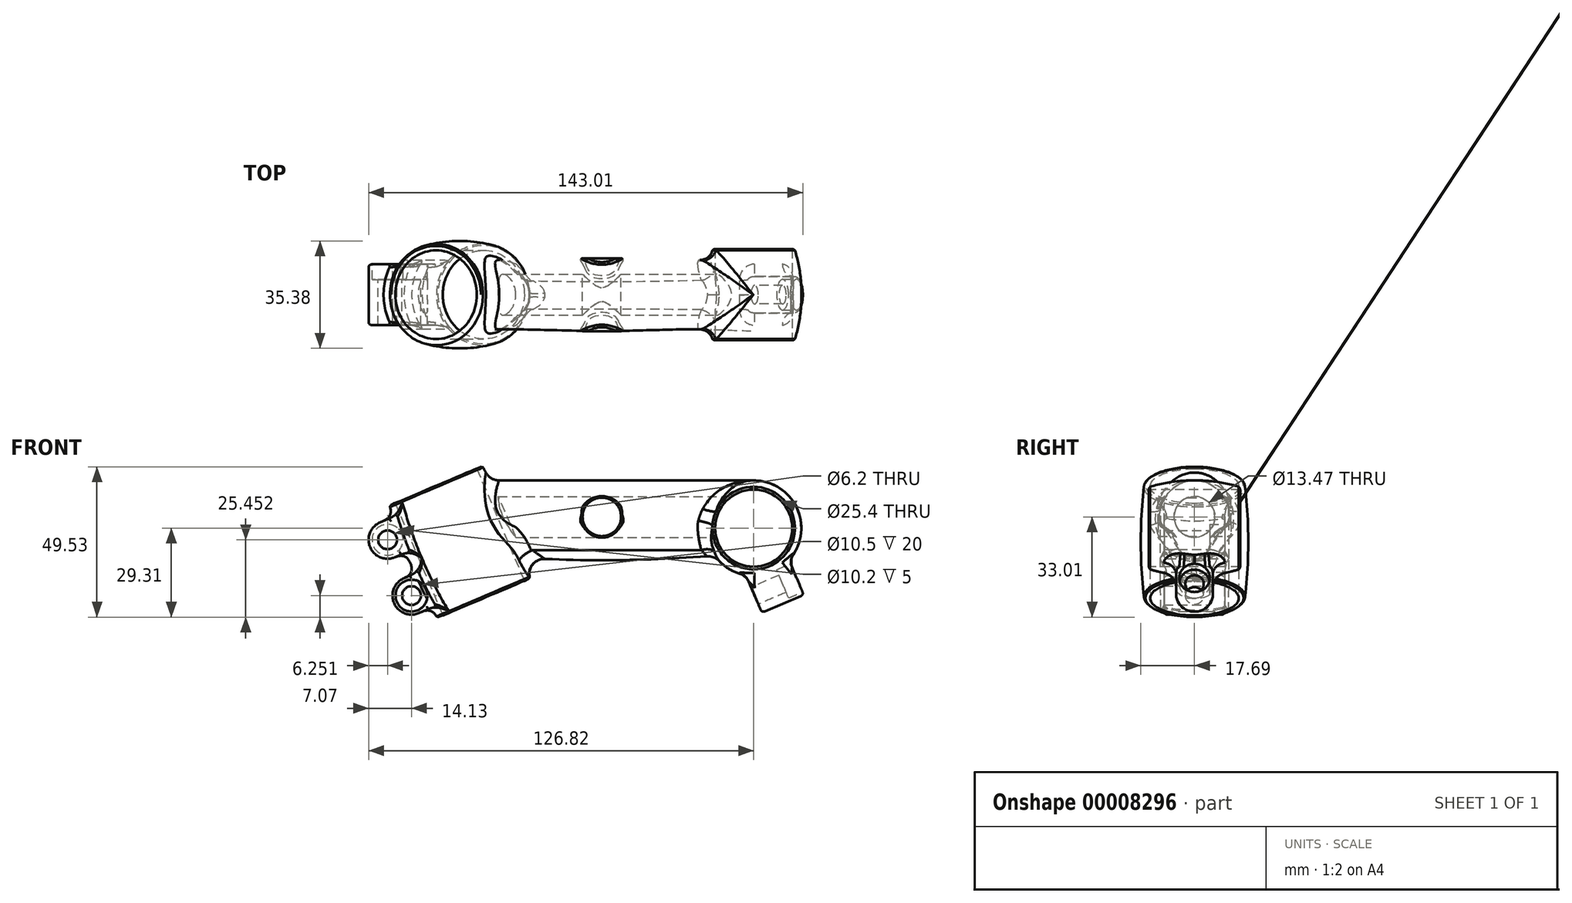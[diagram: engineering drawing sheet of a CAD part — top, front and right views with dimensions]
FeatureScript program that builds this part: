
annotation { "Feature Type Name" : "Feature", "Feature Type Description" : "" }
export const myFeature = defineFeature(function(context is Context, id is Id, definition is map)
    precondition{}
    {
        {
            var Q0;
            Q0=qCreatedBy(makeId("Right.planeOp"),FACE);
            var sketch = newSketch(context, id + "F0", { "sketchPlane" : qUnion([Q0])});
            skArc(sketch, "E0", {"start": v(11.9, 1.57) * mm, "mid": v(-0.17, 12) * mm, "end": v(-11.94, 1.24) * mm});
            skArc(sketch, "E1", {"start": v(-4.75, -11.02) * mm, "mid": v(-5.92, -6.75) * mm, "end": v(-9.19, -3.76) * mm});
            skArc(sketch, "E2.0.MirrorCS", {"start": v(4.18, -11.25) * mm, "mid": v(5.4, -6.72) * mm, "end": v(8.95, -3.66) * mm});
            skArc(sketch, "E3", {"start": v(-4.75, -11.02) * mm, "mid": v(-0.37, -14.28) * mm, "end": v(4.18, -11.25) * mm});
            skPoint(sketch, "E4.visualSharp", {"position": v(-11.62, -3) * mm});
            skArc(sketch, "E4.filletArc", {"start": v(-11.94, 1.24) * mm, "mid": v(-11.34, -1.69) * mm, "end": v(-9.19, -3.76) * mm});
            skPoint(sketch, "E5.visualSharp", {"position": v(11.62, -3) * mm});
            skArc(sketch, "E5.filletArc", {"start": v(8.95, -3.66) * mm, "mid": v(11.3, -1.53) * mm, "end": v(11.9, 1.57) * mm});
            skLineSegment(sketch, "E6", {"start": v(0, -14.28) * mm, "end": v(0, 12) * mm, "construction": true});
            skLineSegment(sketch, "E7", {"start": v(11.85, 0) * mm, "end": v(-11.91, 0) * mm, "construction": true});
            skSolve(sketch);
        }
        {
            var Q0;
            Q0=qCreatedBy(makeId("Right.planeOp"),FACE);
            cPlane(context, id + "F1", {"entities" : qUnion([Q0]), "cplaneType" : CPlaneType.OFFSET, "offset" : 50 * mm, "width" : 150 * mm, "height" : 150 * mm});
        }
        {
            var Q0;
            Q0=qCreatedBy(id+"F1.planeOp",FACE);
            var sketch = newSketch(context, id + "F2", { "sketchPlane" : qUnion([Q0])});
            skCircle(sketch, "E8", {"center": v(0, 0) * mm, "radius": 12 * mm});
            skLineSegment(sketch, "E9", {"start": v(0, -12) * mm, "end": v(0, 12) * mm, "construction": true});
            skLineSegment(sketch, "E10", {"start": v(-12, 0) * mm, "end": v(12, 0) * mm, "construction": true});
            skSolve(sketch);
        }
        {
            var Q0;
            Q0=qCreatedBy(makeId("Right.planeOp"),FACE);
            cPlane(context, id + "F3", {"entities" : qUnion([Q0]), "cplaneType" : CPlaneType.OFFSET, "offset" : 50 * mm, "oppositeDirection" : true, "width" : 150 * mm, "height" : 150 * mm});
        }
        {
            var Q0;
            Q0=qCreatedBy(id+"F3.planeOp",FACE);
            var sketch = newSketch(context, id + "F4", { "sketchPlane" : qUnion([Q0])});
            skCircle(sketch, "E11", {"center": v(0, 0) * mm, "radius": 12 * mm});
            skLineSegment(sketch, "E12", {"start": v(0, -12) * mm, "end": v(0, 12) * mm, "construction": true});
            skLineSegment(sketch, "E13", {"start": v(12, 0) * mm, "end": v(-12, 0) * mm, "construction": true});
            skSolve(sketch);
        }
        {
            var Q0;
            Q0=makeQuery(id+"F2.imprint","IMPRINT",FACE,{"disambiguationData":[TD([[makeQuery(id+"F2.imprint","IMPRINT",EDGE,{"derivedFrom":sQuery(id+"F2.wireOp",EDGE,"E8")}),1.0]])]});
            var Q1;
            Q1=makeQuery(id+"F0.imprint","IMPRINT",FACE,{"disambiguationData":[TD([[makeQuery(id+"F0.imprint","IMPRINT",EDGE,{"derivedFrom":sQuery(id+"F0.wireOp",EDGE,"E0")}),1.0]])]});
            var Q2;
            Q2=makeQuery(id+"F4.imprint","IMPRINT",FACE,{"disambiguationData":[TD([[makeQuery(id+"F4.imprint","IMPRINT",EDGE,{"derivedFrom":sQuery(id+"F4.wireOp",EDGE,"E11")}),1.0]])]});
            var Q3;
            Q3=sQuery(id+"F4.wireOp",VERTEX,"E12.end");
            var Q4;
            Q4=sQuery(id+"F0.wireOp",VERTEX,"E6.end");
            var Q5;
            Q5=sQuery(id+"F2.wireOp",VERTEX,"E9.end");
            loft(context, id + "F5", {"sheetProfilesArray" : [{ "sheetProfileEntities" : qUnion([Q0]) }, { "sheetProfileEntities" : qUnion([Q1]) }, { "sheetProfileEntities" : qUnion([Q2]) }], "matchConnections" : true, "connections" : [{ "connectionEntities" : qUnion([Q3, Q4, Q5]), "connectionEdgeQueries" : qUnion([]), "connectionEdgeParameters" : [] }]});
        }
        {
            var Q0;
            Q0=qCreatedBy(id+"F1.planeOp",FACE);
            var sketch = newSketch(context, id + "F6", { "sketchPlane" : qUnion([Q0])});
            skLineSegment(sketch, "E14", {"start": v(0, 0) * mm, "end": v(0, 7) * mm});
            skLineSegment(sketch, "E15.0", {"start": v(0, 9) * mm, "end": v(15, 9) * mm, "construction": true});
            skLineSegment(sketch, "E16.0", {"start": v(0, -3.7) * mm, "end": v(30.55, -3.7) * mm});
            skPoint(sketch, "E17.start.orphan", {"position": v(0, 14.9) * mm});
            skLineSegment(sketch, "E18", {"start": v(15, 9) * mm, "end": v(15, 7) * mm});
            skArc(sketch, "E19", {"start": v(15, 9) * mm, "mid": v(14.9, 9.49) * mm, "end": v(14.6, 9.9) * mm});
            skArc(sketch, "E20", {"start": v(14.6, 9.9) * mm, "mid": v(7.38, 11.53) * mm, "end": v(0, 12) * mm});
            skLineSegment(sketch, "E21.0", {"start": v(0, 7) * mm, "end": v(15, 7) * mm});
            skArc(sketch, "E22.0.MirrorCS", {"start": v(-14.6, 9.9) * mm, "mid": v(-7.38, 11.53) * mm, "end": v(0, 12) * mm});
            skArc(sketch, "E23.0.MirrorCS", {"start": v(-15, 9) * mm, "mid": v(-14.9, 9.49) * mm, "end": v(-14.6, 9.9) * mm});
            skLineSegment(sketch, "E24.0.MirrorCS", {"start": v(-15, 9) * mm, "end": v(-15, 7) * mm});
            skLineSegment(sketch, "E25.0.MirrorCS", {"start": v(0, 7) * mm, "end": v(-15, 7) * mm});
            skSolve(sketch);
        }
        {
            var Q0;
            Q0 = qSketchRegion(id + "F6", true);
            var Q1;
            Q1=sQuery(id+"F6.wireOp",EDGE,"E16.0");
            revolve(context, id + "F7", {"operationType" : NewBodyOperationType.ADD, "entities" : qUnion([Q0]), "axis" : qUnion([Q1]), "revolveType" : RevolveType.FULL});
        }
        {
            var Q0;
            Q0=makeQuery(id+"F7.opRevolve","SWEPT_FACE",FACE,{"disambiguationData":[OSD([sQuery(id+"F6.wireOp",EDGE,"E24.0.MirrorCS")])]});
            var sketch = newSketch(context, id + "F8", { "sketchPlane" : qUnion([Q0])});
            skCircle(sketch, "E26", {"center": v(50, -3.7) * mm, "radius": 12.7 * mm});
            skSolve(sketch);
        }
        {
            var Q0;
            Q0 = qSketchRegion(id + "F8", true);
            extrude(context, id + "F9", {"entities" : qUnion([Q0]), "operationType" : NewBodyOperationType.REMOVE, "oppositeDirection" : true, "depth" : 30 * mm});
        }
        {
            var Q0;
            Q0=qCreatedBy(makeId("Front.planeOp"),FACE);
            var sketch = newSketch(context, id + "F10", { "sketchPlane" : qUnion([Q0])});
            skLineSegment(sketch, "E27", {"start": v(11.01, 21.07) * mm, "end": v(-86.9, -12.65) * mm});
            skPoint(sketch, "E28.orphan", {"position": v(-50.17, 0) * mm});
            skSolve(sketch);
        }
        {
            var Q0;
            Q0=qCreatedBy(id+"F1.planeOp",FACE);
            var sketch = newSketch(context, id + "F11", { "sketchPlane" : qUnion([Q0])});
            skCircle(sketch, "E29", {"center": v(0, 0) * mm, "radius": 6.73 * mm});
            skSolve(sketch);
        }
        {
            var Q0;
            Q0 = qSketchRegion(id + "F11", true);
            extrude(context, id + "F12", {"entities" : qUnion([Q0]), "operationType" : NewBodyOperationType.REMOVE, "oppositeDirection" : true, "depth" : 100 * mm});
        }
        {
            var Q0;
            Q0=makeQuery(id+"F7.opRevolve","SWEPT_EDGE",EDGE,{"disambiguationData":[OSD([sQuery(id+"F6.wireOp",EDGE,"E20"),sQuery(id+"F6.wireOp",EDGE,"E22.0.MirrorCS")])]});
            var Q1;
            Q1=makeQuery(id+"F7.boolean.opBoolean","INTERSECT",EDGE,{"derivedFrom":[makeQuery(id+"F5.opLoft","SWEPT_FACE",FACE,{"disambiguationData":[OSD([sQuery(id+"F0.wireOp",EDGE,"E1"),sQuery(id+"F0.wireOp",EDGE,"E2.0.MirrorCS"),sQuery(id+"F0.wireOp",EDGE,"E3"),sQuery(id+"F0.wireOp",EDGE,"E4.filletArc"),sQuery(id+"F2.wireOp",EDGE,"E8")])]}),makeQuery(id+"F7.opRevolve","SWEPT_FACE",FACE,{"disambiguationData":[OSD([sQuery(id+"F6.wireOp",EDGE,"E22.0.MirrorCS")])]})]});
            var Q2;
            Q2=makeQuery(id+"F7.boolean.opBoolean","INTERSECT",EDGE,{"derivedFrom":[makeQuery(id+"F5.opLoft","SWEPT_FACE",FACE,{"disambiguationData":[OSD([sQuery(id+"F0.wireOp",EDGE,"E1"),sQuery(id+"F0.wireOp",EDGE,"E2.0.MirrorCS"),sQuery(id+"F0.wireOp",EDGE,"E3"),sQuery(id+"F0.wireOp",EDGE,"E4.filletArc"),sQuery(id+"F2.wireOp",EDGE,"E8")])]}),makeQuery(id+"F7.opRevolve","SWEPT_FACE",FACE,{"disambiguationData":[OSD([sQuery(id+"F6.wireOp",EDGE,"E20")])]})]});
            var Q3;
            Q3=makeQuery(id+"F7.boolean.opBoolean","INTERSECT",EDGE,{"derivedFrom":[makeQuery(id+"F5.opLoft","SWEPT_FACE",FACE,{"disambiguationData":[OSD([sQuery(id+"F0.wireOp",EDGE,"E1"),sQuery(id+"F0.wireOp",EDGE,"E2.0.MirrorCS"),sQuery(id+"F0.wireOp",EDGE,"E3"),sQuery(id+"F0.wireOp",EDGE,"E5.filletArc"),sQuery(id+"F2.wireOp",EDGE,"E8")])]}),makeQuery(id+"F7.opRevolve","SWEPT_FACE",FACE,{"disambiguationData":[OSD([sQuery(id+"F6.wireOp",EDGE,"E22.0.MirrorCS")])]})]});
            var Q4;
            Q4=makeQuery(id+"F7.boolean.opBoolean","INTERSECT",EDGE,{"derivedFrom":[makeQuery(id+"F5.opLoft","SWEPT_FACE",FACE,{"disambiguationData":[OSD([sQuery(id+"F0.wireOp",EDGE,"E1"),sQuery(id+"F0.wireOp",EDGE,"E2.0.MirrorCS"),sQuery(id+"F0.wireOp",EDGE,"E3"),sQuery(id+"F0.wireOp",EDGE,"E5.filletArc"),sQuery(id+"F2.wireOp",EDGE,"E8")])]}),makeQuery(id+"F7.opRevolve","SWEPT_FACE",FACE,{"disambiguationData":[OSD([sQuery(id+"F6.wireOp",EDGE,"E20")])]})]});
            fillet(context, id + "F13", {"entities" : qUnion([Q0, Q1, Q2, Q3, Q4]), "radius" : 5 * mm, "tangentPropagation" : true, "allowEdgeOverflow" : false});
        }
        {
            var Q0;
            Q0=sQuery(id+"F10.wireOp",EDGE,"E27");
            cPlane(context, id + "F14", {"entities" : qUnion([Q0]), "cplaneType" : CPlaneType.LINE_ANGLE, "offset" : 150 * mm, "angle" : 0 * degree, "width" : 150 * mm, "height" : 150 * mm});
        }
        {
            var Q0;
            Q0=qCreatedBy(id+"F14.planeOp",FACE);
            var sketch = newSketch(context, id + "F15", { "sketchPlane" : qUnion([Q0])});
            skLineSegment(sketch, "E30", {"start": v(-34.95, -36.2) * mm, "end": v(-56.16, 13.8) * mm});
            skPoint(sketch, "E31.orphan", {"position": v(-50.3, 0) * mm});
            skLineSegment(sketch, "E32.0", {"start": v(12.64, 16.34) * mm, "end": v(-85.27, -17.37) * mm, "construction": true});
            skLineSegment(sketch, "E33.0", {"start": v(-68.04, 4.42) * mm, "end": v(-69.93, 3.77) * mm});
            skLineSegment(sketch, "E34.0", {"start": v(-52.38, -32.49) * mm, "end": v(-54.27, -33.14) * mm});
            skLineSegment(sketch, "E35", {"start": v(-68.04, 4.42) * mm, "end": v(-52.38, -32.49) * mm, "construction": true});
            skArc(sketch, "E36", {"start": v(-69.93, 3.77) * mm, "mid": v(-63.11, -15.11) * mm, "end": v(-54.27, -33.14) * mm});
            skLineSegment(sketch, "E37", {"start": v(-52.38, -32.49) * mm, "end": v(-38.94, -26.79) * mm});
            skLineSegment(sketch, "E38", {"start": v(-68.04, 4.42) * mm, "end": v(-54.6, 10.12) * mm});
            skSolve(sketch);
        }
        {
            var Q0;
            Q0 = qSketchRegion(id + "F15", true);
            var Q1;
            Q1=sQuery(id+"F15.wireOp",EDGE,"E30");
            revolve(context, id + "F16", {"operationType" : NewBodyOperationType.ADD, "entities" : qUnion([Q0]), "axis" : qUnion([Q1]), "revolveType" : RevolveType.FULL});
        }
        {
            var Q0;
            Q0=makeQuery(id+"F16.opRevolve","SWEPT_FACE",FACE,{"disambiguationData":[OSD([sQuery(id+"F15.wireOp",EDGE,"E33.0")])]});
            cPlane(context, id + "F17", {"entities" : qUnion([Q0]), "cplaneType" : CPlaneType.LINE_ANGLE, "offset" : 5 * mm, "angle" : 180 * degree, "width" : 150 * mm, "height" : 150 * mm});
        }
        {
            var Q0;
            Q0=qCreatedBy(id+"F14.planeOp",FACE);
            var sketch = newSketch(context, id + "F18", { "sketchPlane" : qUnion([Q0])});
            skLineSegment(sketch, "E39", {"start": v(-69.95, 3.7) * mm, "end": v(-54.11, -33.26) * mm, "construction": true});
            skLineSegment(sketch, "E40", {"start": v(-57.44, -12.8) * mm, "end": v(-62.03, -14.78) * mm});
            skLineSegment(sketch, "E41.0", {"start": v(-61.38, -3.62) * mm, "end": v(-65.97, -5.59) * mm});
            skLineSegment(sketch, "E42.0", {"start": v(-74.55, 1.73) * mm, "end": v(-58.7, -35.23) * mm, "construction": true});
            skCircle(sketch, "E43", {"center": v(-70.57, -7.56) * mm, "radius": 3.1 * mm});
            skCircle(sketch, "E44", {"center": v(-70.57, -7.56) * mm, "radius": 5.25 * mm});
            skLineSegment(sketch, "E45.0", {"start": v(-65.36, 5.67) * mm, "end": v(-49.52, -31.29) * mm});
            skCircle(sketch, "E46.0", {"center": v(-70.57, -7.56) * mm, "radius": 6.25 * mm});
            skCircle(sketch, "E47.2.MirrorC", {"center": v(-62.69, -25.94) * mm, "radius": 3.1 * mm});
            skCircle(sketch, "E47.3.MirrorC", {"center": v(-62.69, -25.94) * mm, "radius": 5.25 * mm});
            skCircle(sketch, "E47.4.MirrorC", {"center": v(-62.69, -25.94) * mm, "radius": 6.25 * mm});
            skLineSegment(sketch, "E48", {"start": v(-73.03, -1.81) * mm, "end": v(-63.84, 2.13) * mm});
            skLineSegment(sketch, "E49", {"start": v(-65.15, -20.2) * mm, "end": v(-55.96, -16.26) * mm});
            skLineSegment(sketch, "E50", {"start": v(-60.23, -31.68) * mm, "end": v(-51.04, -27.75) * mm});
            skLineSegment(sketch, "E51", {"start": v(-68.1, -13.3) * mm, "end": v(-58.92, -9.36) * mm});
            skSolve(sketch);
        }
        {
            var Q0;
            Q0 = qSketchRegion(id + "F18", true);
            var Q1;
            Q1=makeQuery(id+"F18.imprint","IMPRINT",FACE,{"disambiguationData":[TD([[makeQuery(id+"F18.imprint","IMPRINT",EDGE,{"derivedFrom":sQuery(id+"F18.wireOp",EDGE,"E43")}),-1.0]])]});
            var Q2;
            Q2=makeQuery(id+"F18.imprint","IMPRINT",FACE,{"disambiguationData":[TD([[makeQuery(id+"F18.imprint","IMPRINT",EDGE,{"derivedFrom":sQuery(id+"F18.wireOp",EDGE,"E47.2.MirrorC")}),1.0]])]});
            extrude(context, id + "F19", {"entities" : qUnion([Q0, Q1, Q2]), "operationType" : NewBodyOperationType.ADD, "endBound" : BoundingType.SYMMETRIC, "depth" : 20 * mm});
        }
        {
            var Q0;
            Q0=makeQuery(id+"F19.boolean.opBoolean","INTERSECT",EDGE,{"derivedFrom":[makeQuery(id+"F16.boolean.opBoolean","SPLIT",FACE,{"disambiguationData":[TD([makeQuery(id+"F16.opRevolve","SWEPT_FACE",FACE,{"disambiguationData":[OSD([sQuery(id+"F15.wireOp",EDGE,"E33.0")])]})])],"derivedFrom":makeQuery(id+"F16.opRevolve","SWEPT_FACE",FACE,{"disambiguationData":[OSD([sQuery(id+"F15.wireOp",EDGE,"E36")])]})}),makeQuery(id+"F19.opExtrude","SWEPT_FACE",FACE,{"disambiguationData":[OSD([sQuery(id+"F18.wireOp",EDGE,"E49")])]})]});
            var Q1;
            Q1=makeQuery(id+"F19.boolean.opBoolean","INTERSECT",EDGE,{"derivedFrom":[makeQuery(id+"F16.boolean.opBoolean","SPLIT",FACE,{"disambiguationData":[TD([makeQuery(id+"F16.opRevolve","SWEPT_FACE",FACE,{"disambiguationData":[OSD([sQuery(id+"F15.wireOp",EDGE,"E33.0")])]})])],"derivedFrom":makeQuery(id+"F16.opRevolve","SWEPT_FACE",FACE,{"disambiguationData":[OSD([sQuery(id+"F15.wireOp",EDGE,"E36")])]})}),makeQuery(id+"F19.opExtrude","CAP_FACE",FACE,{"disambiguationData":[OSD([sQuery(id+"F18.wireOp",EDGE,"E45.0"),sQuery(id+"F18.wireOp",EDGE,"E47.2.MirrorC"),sQuery(id+"F18.wireOp",EDGE,"E47.4.MirrorC"),sQuery(id+"F18.wireOp",EDGE,"E49"),sQuery(id+"F18.wireOp",EDGE,"E50")])],"isStart":false})]});
            var Q2;
            Q2=makeQuery(id+"F19.boolean.opBoolean","INTERSECT",EDGE,{"derivedFrom":[makeQuery(id+"F16.boolean.opBoolean","SPLIT",FACE,{"disambiguationData":[TD([makeQuery(id+"F16.opRevolve","SWEPT_FACE",FACE,{"disambiguationData":[OSD([sQuery(id+"F15.wireOp",EDGE,"E33.0")])]})])],"derivedFrom":makeQuery(id+"F16.opRevolve","SWEPT_FACE",FACE,{"disambiguationData":[OSD([sQuery(id+"F15.wireOp",EDGE,"E36")])]})}),makeQuery(id+"F19.opExtrude","SWEPT_FACE",FACE,{"disambiguationData":[OSD([sQuery(id+"F18.wireOp",EDGE,"E50")])]})]});
            var Q3;
            Q3=makeQuery(id+"F19.boolean.opBoolean","INTERSECT",EDGE,{"derivedFrom":[makeQuery(id+"F16.boolean.opBoolean","SPLIT",FACE,{"disambiguationData":[TD([makeQuery(id+"F16.opRevolve","SWEPT_FACE",FACE,{"disambiguationData":[OSD([sQuery(id+"F15.wireOp",EDGE,"E33.0")])]})])],"derivedFrom":makeQuery(id+"F16.opRevolve","SWEPT_FACE",FACE,{"disambiguationData":[OSD([sQuery(id+"F15.wireOp",EDGE,"E36")])]})}),makeQuery(id+"F19.opExtrude","CAP_FACE",FACE,{"disambiguationData":[OSD([sQuery(id+"F18.wireOp",EDGE,"E45.0"),sQuery(id+"F18.wireOp",EDGE,"E47.2.MirrorC"),sQuery(id+"F18.wireOp",EDGE,"E47.4.MirrorC"),sQuery(id+"F18.wireOp",EDGE,"E49"),sQuery(id+"F18.wireOp",EDGE,"E50")])],"isStart":true})]});
            fillet(context, id + "F20", {"entities" : qUnion([Q0, Q1, Q2, Q3]), "radius" : 3.75 * mm, "tangentPropagation" : true, "rho" : 0.5, "crossSection" : FilletCrossSection.CONIC, "allowEdgeOverflow" : false});
        }
        {
            var Q0;
            Q0=makeQuery(id+"F19.boolean.opBoolean","INTERSECT",EDGE,{"derivedFrom":[makeQuery(id+"F16.boolean.opBoolean","SPLIT",FACE,{"disambiguationData":[TD([makeQuery(id+"F16.opRevolve","SWEPT_FACE",FACE,{"disambiguationData":[OSD([sQuery(id+"F15.wireOp",EDGE,"E33.0")])]})])],"derivedFrom":makeQuery(id+"F16.opRevolve","SWEPT_FACE",FACE,{"disambiguationData":[OSD([sQuery(id+"F15.wireOp",EDGE,"E36")])]})}),makeQuery(id+"F19.opExtrude","SWEPT_FACE",FACE,{"disambiguationData":[OSD([sQuery(id+"F18.wireOp",EDGE,"E48")])]})]});
            var Q1;
            Q1=makeQuery(id+"F19.boolean.opBoolean","INTERSECT",EDGE,{"derivedFrom":[makeQuery(id+"F16.boolean.opBoolean","SPLIT",FACE,{"disambiguationData":[TD([makeQuery(id+"F16.opRevolve","SWEPT_FACE",FACE,{"disambiguationData":[OSD([sQuery(id+"F15.wireOp",EDGE,"E33.0")])]})])],"derivedFrom":makeQuery(id+"F16.opRevolve","SWEPT_FACE",FACE,{"disambiguationData":[OSD([sQuery(id+"F15.wireOp",EDGE,"E36")])]})}),makeQuery(id+"F19.opExtrude","CAP_FACE",FACE,{"disambiguationData":[OSD([sQuery(id+"F18.wireOp",EDGE,"E43"),sQuery(id+"F18.wireOp",EDGE,"E45.0"),sQuery(id+"F18.wireOp",EDGE,"E46.0"),sQuery(id+"F18.wireOp",EDGE,"E48"),sQuery(id+"F18.wireOp",EDGE,"E51")])],"isStart":false})]});
            var Q2;
            Q2=makeQuery(id+"F19.boolean.opBoolean","INTERSECT",EDGE,{"derivedFrom":[makeQuery(id+"F16.boolean.opBoolean","SPLIT",FACE,{"disambiguationData":[TD([makeQuery(id+"F16.opRevolve","SWEPT_FACE",FACE,{"disambiguationData":[OSD([sQuery(id+"F15.wireOp",EDGE,"E33.0")])]})])],"derivedFrom":makeQuery(id+"F16.opRevolve","SWEPT_FACE",FACE,{"disambiguationData":[OSD([sQuery(id+"F15.wireOp",EDGE,"E36")])]})}),makeQuery(id+"F19.opExtrude","SWEPT_FACE",FACE,{"disambiguationData":[OSD([sQuery(id+"F18.wireOp",EDGE,"E51")])]})]});
            var Q3;
            Q3=makeQuery(id+"F19.boolean.opBoolean","INTERSECT",EDGE,{"derivedFrom":[makeQuery(id+"F16.boolean.opBoolean","SPLIT",FACE,{"disambiguationData":[TD([makeQuery(id+"F16.opRevolve","SWEPT_FACE",FACE,{"disambiguationData":[OSD([sQuery(id+"F15.wireOp",EDGE,"E33.0")])]})])],"derivedFrom":makeQuery(id+"F16.opRevolve","SWEPT_FACE",FACE,{"disambiguationData":[OSD([sQuery(id+"F15.wireOp",EDGE,"E36")])]})}),makeQuery(id+"F19.opExtrude","CAP_FACE",FACE,{"disambiguationData":[OSD([sQuery(id+"F18.wireOp",EDGE,"E43"),sQuery(id+"F18.wireOp",EDGE,"E45.0"),sQuery(id+"F18.wireOp",EDGE,"E46.0"),sQuery(id+"F18.wireOp",EDGE,"E48"),sQuery(id+"F18.wireOp",EDGE,"E51")])],"isStart":true})]});
            fillet(context, id + "F21", {"entities" : qUnion([Q0, Q1, Q2, Q3]), "radius" : 3.75 * mm, "tangentPropagation" : true, "rho" : 0.5, "crossSection" : FilletCrossSection.CONIC, "allowEdgeOverflow" : false});
        }
        {
            var Q0;
            {var subQ0=sQuery(id+"F0.wireOp",EDGE,"E1");var subQ1=sQuery(id+"F0.wireOp",EDGE,"E2.0.MirrorCS");var subQ2=sQuery(id+"F0.wireOp",EDGE,"E3");var subQ3=sQuery(id+"F2.wireOp",EDGE,"E8");Q0=makeQuery(id+"F16.boolean.opBoolean","INTERSECT",EDGE,{"derivedFrom":[makeQuery(id+"F7.boolean.opBoolean","SPLIT",FACE,{"disambiguationData":[TD([makeQuery(id+"F5.opLoft","SWEPT_FACE",FACE,{"disambiguationData":[OSD([subQ0,subQ1,subQ2,sQuery(id+"F0.wireOp",EDGE,"E5.filletArc"),subQ3])]}),makeQuery(id+"F5.opLoft","CAP_FACE",FACE,{"disambiguationData":[OSD([makeQuery(id+"F4.imprint","IMPRINT",FACE,{"disambiguationData":[TD([[makeQuery(id+"F4.imprint","IMPRINT",EDGE,{"derivedFrom":sQuery(id+"F4.wireOp",EDGE,"E11")}),1.0]])]})])],"isStart":true}),makeQuery(id+"F7.opRevolve","SWEPT_FACE",FACE,{"disambiguationData":[OSD([sQuery(id+"F6.wireOp",EDGE,"E20")])]}),makeQuery(id+"F7.opRevolve","SWEPT_FACE",FACE,{"disambiguationData":[OSD([sQuery(id+"F6.wireOp",EDGE,"E22.0.MirrorCS")])]})])],"derivedFrom":makeQuery(id+"F5.opLoft","SWEPT_FACE",FACE,{"disambiguationData":[OSD([subQ0,subQ1,subQ2,sQuery(id+"F0.wireOp",EDGE,"E4.filletArc"),subQ3])]})}),makeQuery(id+"F16.opRevolve","SWEPT_FACE",FACE,{"disambiguationData":[OSD([sQuery(id+"F15.wireOp",EDGE,"E36")])]})]});}
            var Q1;
            {var subQ0=sQuery(id+"F0.wireOp",EDGE,"E1");var subQ1=sQuery(id+"F0.wireOp",EDGE,"E2.0.MirrorCS");var subQ2=sQuery(id+"F0.wireOp",EDGE,"E3");var subQ3=sQuery(id+"F2.wireOp",EDGE,"E8");Q1=makeQuery(id+"F16.boolean.opBoolean","INTERSECT",EDGE,{"derivedFrom":[makeQuery(id+"F7.boolean.opBoolean","SPLIT",FACE,{"disambiguationData":[TD([makeQuery(id+"F5.opLoft","CAP_FACE",FACE,{"disambiguationData":[OSD([makeQuery(id+"F4.imprint","IMPRINT",FACE,{"disambiguationData":[TD([[makeQuery(id+"F4.imprint","IMPRINT",EDGE,{"derivedFrom":sQuery(id+"F4.wireOp",EDGE,"E11")}),1.0]])]})])],"isStart":true})])],"derivedFrom":makeQuery(id+"F5.opLoft","SWEPT_FACE",FACE,{"disambiguationData":[OSD([subQ0,subQ1,subQ2,sQuery(id+"F0.wireOp",EDGE,"E5.filletArc"),subQ3])]})}),makeQuery(id+"F16.opRevolve","SWEPT_FACE",FACE,{"disambiguationData":[OSD([sQuery(id+"F15.wireOp",EDGE,"E36")])]})]});}
            fillet(context, id + "F22", {"entities" : qUnion([Q0, Q1]), "radius" : 5 * mm, "tangentPropagation" : true, "allowEdgeOverflow" : false});
        }
        {
            var Q0;
            Q0=makeQuery(id+"F16.opRevolve","SWEPT_FACE",FACE,{"disambiguationData":[OSD([sQuery(id+"F15.wireOp",EDGE,"E37")])]});
            extrude(context, id + "F23", {"entities" : qUnion([Q0]), "operationType" : NewBodyOperationType.REMOVE, "endBound" : BoundingType.THROUGH_ALL, "oppositeDirection" : true, "depth" : 25 * mm});
        }
        {
            var Q0;
            Q0=makeQuery(id+"F19.opExtrude","CAP_EDGE",EDGE,{"disambiguationData":[OSD([sQuery(id+"F18.wireOp",EDGE,"E46.0")])],"isStart":false});
            var Q1;
            Q1=makeQuery(id+"F19.opExtrude","CAP_EDGE",EDGE,{"disambiguationData":[OSD([sQuery(id+"F18.wireOp",EDGE,"E48")])],"isStart":false});
            var Q2;
            {var subQ4=sQuery(id+"F18.wireOp",EDGE,"E48");Q2=makeQuery(id+"F21.opFillet","BLEND_EDGE",EDGE,{"blendedFrom":[makeQuery(id+"F19.boolean.opBoolean","INTERSECT",EDGE,{"derivedFrom":[makeQuery(id+"F16.boolean.opBoolean","SPLIT",FACE,{"disambiguationData":[TD([makeQuery(id+"F16.opRevolve","SWEPT_FACE",FACE,{"disambiguationData":[OSD([sQuery(id+"F15.wireOp",EDGE,"E33.0")])]})])],"derivedFrom":makeQuery(id+"F16.opRevolve","SWEPT_FACE",FACE,{"disambiguationData":[OSD([sQuery(id+"F15.wireOp",EDGE,"E36")])]})}),makeQuery(id+"F19.opExtrude","SWEPT_FACE",FACE,{"disambiguationData":[OSD([subQ4])]})]}),makeQuery(id+"F19.opExtrude","CAP_FACE",FACE,{"disambiguationData":[OSD([sQuery(id+"F18.wireOp",EDGE,"E43"),sQuery(id+"F18.wireOp",EDGE,"E45.0"),sQuery(id+"F18.wireOp",EDGE,"E46.0"),subQ4,sQuery(id+"F18.wireOp",EDGE,"E51")])],"isStart":false})],"blendedInto":[makeQuery(id+"F19.opExtrude","CAP_FACE",FACE,{"disambiguationData":[OSD([sQuery(id+"F18.wireOp",EDGE,"E43"),sQuery(id+"F18.wireOp",EDGE,"E45.0"),sQuery(id+"F18.wireOp",EDGE,"E46.0"),subQ4,sQuery(id+"F18.wireOp",EDGE,"E51")])],"isStart":false})]});}
            var Q3;
            {var subQ4=makeQuery(id+"F16.boolean.opBoolean","SPLIT",FACE,{"disambiguationData":[TD([makeQuery(id+"F16.opRevolve","SWEPT_FACE",FACE,{"disambiguationData":[OSD([sQuery(id+"F15.wireOp",EDGE,"E33.0")])]})])],"derivedFrom":makeQuery(id+"F16.opRevolve","SWEPT_FACE",FACE,{"disambiguationData":[OSD([sQuery(id+"F15.wireOp",EDGE,"E36")])]})});var subQ5=sQuery(id+"F18.wireOp",EDGE,"E48");Q3=makeQuery(id+"F21.opFillet","BLEND_EDGE",EDGE,{"blendedFrom":[makeQuery(id+"F19.boolean.opBoolean","INTERSECT",EDGE,{"derivedFrom":[subQ4,makeQuery(id+"F19.opExtrude","CAP_FACE",FACE,{"disambiguationData":[OSD([sQuery(id+"F18.wireOp",EDGE,"E43"),sQuery(id+"F18.wireOp",EDGE,"E45.0"),sQuery(id+"F18.wireOp",EDGE,"E46.0"),subQ5,sQuery(id+"F18.wireOp",EDGE,"E51")])],"isStart":false})]}),makeQuery(id+"F19.boolean.opBoolean","INTERSECT",EDGE,{"derivedFrom":[subQ4,makeQuery(id+"F19.opExtrude","SWEPT_FACE",FACE,{"disambiguationData":[OSD([subQ5])]})]})],"blendedInto":[]});}
            var Q4;
            Q4=makeQuery(id+"F19.opExtrude","CAP_EDGE",EDGE,{"disambiguationData":[OSD([sQuery(id+"F18.wireOp",EDGE,"E51")])],"isStart":false});
            var Q5;
            {var subQ4=sQuery(id+"F18.wireOp",EDGE,"E51");Q5=makeQuery(id+"F21.opFillet","BLEND_EDGE",EDGE,{"blendedFrom":[makeQuery(id+"F19.boolean.opBoolean","INTERSECT",EDGE,{"derivedFrom":[makeQuery(id+"F16.boolean.opBoolean","SPLIT",FACE,{"disambiguationData":[TD([makeQuery(id+"F16.opRevolve","SWEPT_FACE",FACE,{"disambiguationData":[OSD([sQuery(id+"F15.wireOp",EDGE,"E33.0")])]})])],"derivedFrom":makeQuery(id+"F16.opRevolve","SWEPT_FACE",FACE,{"disambiguationData":[OSD([sQuery(id+"F15.wireOp",EDGE,"E36")])]})}),makeQuery(id+"F19.opExtrude","SWEPT_FACE",FACE,{"disambiguationData":[OSD([subQ4])]})]}),makeQuery(id+"F19.opExtrude","CAP_FACE",FACE,{"disambiguationData":[OSD([sQuery(id+"F18.wireOp",EDGE,"E43"),sQuery(id+"F18.wireOp",EDGE,"E45.0"),sQuery(id+"F18.wireOp",EDGE,"E46.0"),sQuery(id+"F18.wireOp",EDGE,"E48"),subQ4])],"isStart":false})],"blendedInto":[makeQuery(id+"F19.opExtrude","CAP_FACE",FACE,{"disambiguationData":[OSD([sQuery(id+"F18.wireOp",EDGE,"E43"),sQuery(id+"F18.wireOp",EDGE,"E45.0"),sQuery(id+"F18.wireOp",EDGE,"E46.0"),sQuery(id+"F18.wireOp",EDGE,"E48"),subQ4])],"isStart":false})]});}
            var Q6;
            {var subQ4=makeQuery(id+"F16.boolean.opBoolean","SPLIT",FACE,{"disambiguationData":[TD([makeQuery(id+"F16.opRevolve","SWEPT_FACE",FACE,{"disambiguationData":[OSD([sQuery(id+"F15.wireOp",EDGE,"E33.0")])]})])],"derivedFrom":makeQuery(id+"F16.opRevolve","SWEPT_FACE",FACE,{"disambiguationData":[OSD([sQuery(id+"F15.wireOp",EDGE,"E36")])]})});var subQ5=sQuery(id+"F18.wireOp",EDGE,"E51");Q6=makeQuery(id+"F21.opFillet","BLEND_EDGE",EDGE,{"blendedFrom":[makeQuery(id+"F19.boolean.opBoolean","INTERSECT",EDGE,{"derivedFrom":[subQ4,makeQuery(id+"F19.opExtrude","CAP_FACE",FACE,{"disambiguationData":[OSD([sQuery(id+"F18.wireOp",EDGE,"E43"),sQuery(id+"F18.wireOp",EDGE,"E45.0"),sQuery(id+"F18.wireOp",EDGE,"E46.0"),sQuery(id+"F18.wireOp",EDGE,"E48"),subQ5])],"isStart":false})]}),makeQuery(id+"F19.boolean.opBoolean","INTERSECT",EDGE,{"derivedFrom":[subQ4,makeQuery(id+"F19.opExtrude","SWEPT_FACE",FACE,{"disambiguationData":[OSD([subQ5])]})]})],"blendedInto":[]});}
            fillet(context, id + "F24", {"entities" : qUnion([Q0, Q1, Q2, Q3, Q4, Q5, Q6]), "radius" : 1 * mm, "tangentPropagation" : true, "allowEdgeOverflow" : false});
        }
        {
            var Q0;
            {var subQ4=makeQuery(id+"F16.boolean.opBoolean","SPLIT",FACE,{"disambiguationData":[TD([makeQuery(id+"F16.opRevolve","SWEPT_FACE",FACE,{"disambiguationData":[OSD([sQuery(id+"F15.wireOp",EDGE,"E33.0")])]})])],"derivedFrom":makeQuery(id+"F16.opRevolve","SWEPT_FACE",FACE,{"disambiguationData":[OSD([sQuery(id+"F15.wireOp",EDGE,"E36")])]})});var subQ5=sQuery(id+"F18.wireOp",EDGE,"E49");Q0=makeQuery(id+"F20.opFillet","BLEND_EDGE",EDGE,{"blendedFrom":[makeQuery(id+"F19.boolean.opBoolean","INTERSECT",EDGE,{"derivedFrom":[subQ4,makeQuery(id+"F19.opExtrude","CAP_FACE",FACE,{"disambiguationData":[OSD([sQuery(id+"F18.wireOp",EDGE,"E45.0"),sQuery(id+"F18.wireOp",EDGE,"E47.2.MirrorC"),sQuery(id+"F18.wireOp",EDGE,"E47.4.MirrorC"),subQ5,sQuery(id+"F18.wireOp",EDGE,"E50")])],"isStart":false})]}),makeQuery(id+"F19.boolean.opBoolean","INTERSECT",EDGE,{"derivedFrom":[subQ4,makeQuery(id+"F19.opExtrude","SWEPT_FACE",FACE,{"disambiguationData":[OSD([subQ5])]})]})],"blendedInto":[]});}
            var Q1;
            {var subQ4=sQuery(id+"F18.wireOp",EDGE,"E49");Q1=makeQuery(id+"F20.opFillet","BLEND_EDGE",EDGE,{"blendedFrom":[makeQuery(id+"F19.boolean.opBoolean","INTERSECT",EDGE,{"derivedFrom":[makeQuery(id+"F16.boolean.opBoolean","SPLIT",FACE,{"disambiguationData":[TD([makeQuery(id+"F16.opRevolve","SWEPT_FACE",FACE,{"disambiguationData":[OSD([sQuery(id+"F15.wireOp",EDGE,"E33.0")])]})])],"derivedFrom":makeQuery(id+"F16.opRevolve","SWEPT_FACE",FACE,{"disambiguationData":[OSD([sQuery(id+"F15.wireOp",EDGE,"E36")])]})}),makeQuery(id+"F19.opExtrude","SWEPT_FACE",FACE,{"disambiguationData":[OSD([subQ4])]})]}),makeQuery(id+"F19.opExtrude","CAP_FACE",FACE,{"disambiguationData":[OSD([sQuery(id+"F18.wireOp",EDGE,"E45.0"),sQuery(id+"F18.wireOp",EDGE,"E47.2.MirrorC"),sQuery(id+"F18.wireOp",EDGE,"E47.4.MirrorC"),subQ4,sQuery(id+"F18.wireOp",EDGE,"E50")])],"isStart":false})],"blendedInto":[makeQuery(id+"F19.opExtrude","CAP_FACE",FACE,{"disambiguationData":[OSD([sQuery(id+"F18.wireOp",EDGE,"E45.0"),sQuery(id+"F18.wireOp",EDGE,"E47.2.MirrorC"),sQuery(id+"F18.wireOp",EDGE,"E47.4.MirrorC"),subQ4,sQuery(id+"F18.wireOp",EDGE,"E50")])],"isStart":false})]});}
            var Q2;
            Q2=makeQuery(id+"F19.opExtrude","CAP_EDGE",EDGE,{"disambiguationData":[OSD([sQuery(id+"F18.wireOp",EDGE,"E49")])],"isStart":false});
            var Q3;
            Q3=makeQuery(id+"F19.opExtrude","CAP_EDGE",EDGE,{"disambiguationData":[OSD([sQuery(id+"F18.wireOp",EDGE,"E47.4.MirrorC")])],"isStart":false});
            var Q4;
            Q4=makeQuery(id+"F19.opExtrude","CAP_EDGE",EDGE,{"disambiguationData":[OSD([sQuery(id+"F18.wireOp",EDGE,"E50")])],"isStart":false});
            var Q5;
            {var subQ4=sQuery(id+"F18.wireOp",EDGE,"E50");Q5=makeQuery(id+"F20.opFillet","BLEND_EDGE",EDGE,{"blendedFrom":[makeQuery(id+"F19.boolean.opBoolean","INTERSECT",EDGE,{"derivedFrom":[makeQuery(id+"F16.boolean.opBoolean","SPLIT",FACE,{"disambiguationData":[TD([makeQuery(id+"F16.opRevolve","SWEPT_FACE",FACE,{"disambiguationData":[OSD([sQuery(id+"F15.wireOp",EDGE,"E33.0")])]})])],"derivedFrom":makeQuery(id+"F16.opRevolve","SWEPT_FACE",FACE,{"disambiguationData":[OSD([sQuery(id+"F15.wireOp",EDGE,"E36")])]})}),makeQuery(id+"F19.opExtrude","SWEPT_FACE",FACE,{"disambiguationData":[OSD([subQ4])]})]}),makeQuery(id+"F19.opExtrude","CAP_FACE",FACE,{"disambiguationData":[OSD([sQuery(id+"F18.wireOp",EDGE,"E45.0"),sQuery(id+"F18.wireOp",EDGE,"E47.2.MirrorC"),sQuery(id+"F18.wireOp",EDGE,"E47.4.MirrorC"),sQuery(id+"F18.wireOp",EDGE,"E49"),subQ4])],"isStart":false})],"blendedInto":[makeQuery(id+"F19.opExtrude","CAP_FACE",FACE,{"disambiguationData":[OSD([sQuery(id+"F18.wireOp",EDGE,"E45.0"),sQuery(id+"F18.wireOp",EDGE,"E47.2.MirrorC"),sQuery(id+"F18.wireOp",EDGE,"E47.4.MirrorC"),sQuery(id+"F18.wireOp",EDGE,"E49"),subQ4])],"isStart":false})]});}
            var Q6;
            {var subQ4=makeQuery(id+"F16.boolean.opBoolean","SPLIT",FACE,{"disambiguationData":[TD([makeQuery(id+"F16.opRevolve","SWEPT_FACE",FACE,{"disambiguationData":[OSD([sQuery(id+"F15.wireOp",EDGE,"E33.0")])]})])],"derivedFrom":makeQuery(id+"F16.opRevolve","SWEPT_FACE",FACE,{"disambiguationData":[OSD([sQuery(id+"F15.wireOp",EDGE,"E36")])]})});var subQ5=sQuery(id+"F18.wireOp",EDGE,"E50");Q6=makeQuery(id+"F20.opFillet","BLEND_EDGE",EDGE,{"blendedFrom":[makeQuery(id+"F19.boolean.opBoolean","INTERSECT",EDGE,{"derivedFrom":[subQ4,makeQuery(id+"F19.opExtrude","CAP_FACE",FACE,{"disambiguationData":[OSD([sQuery(id+"F18.wireOp",EDGE,"E45.0"),sQuery(id+"F18.wireOp",EDGE,"E47.2.MirrorC"),sQuery(id+"F18.wireOp",EDGE,"E47.4.MirrorC"),sQuery(id+"F18.wireOp",EDGE,"E49"),subQ5])],"isStart":false})]}),makeQuery(id+"F19.boolean.opBoolean","INTERSECT",EDGE,{"derivedFrom":[subQ4,makeQuery(id+"F19.opExtrude","SWEPT_FACE",FACE,{"disambiguationData":[OSD([subQ5])]})]})],"blendedInto":[]});}
            fillet(context, id + "F25", {"entities" : qUnion([Q0, Q1, Q2, Q3, Q4, Q5, Q6]), "radius" : 1 * mm, "tangentPropagation" : true, "allowEdgeOverflow" : false});
        }
        {
            var Q0;
            {var subQ4=makeQuery(id+"F16.boolean.opBoolean","SPLIT",FACE,{"disambiguationData":[TD([makeQuery(id+"F16.opRevolve","SWEPT_FACE",FACE,{"disambiguationData":[OSD([sQuery(id+"F15.wireOp",EDGE,"E33.0")])]})])],"derivedFrom":makeQuery(id+"F16.opRevolve","SWEPT_FACE",FACE,{"disambiguationData":[OSD([sQuery(id+"F15.wireOp",EDGE,"E36")])]})});var subQ5=sQuery(id+"F18.wireOp",EDGE,"E48");Q0=makeQuery(id+"F21.opFillet","BLEND_EDGE",EDGE,{"blendedFrom":[makeQuery(id+"F19.boolean.opBoolean","INTERSECT",EDGE,{"derivedFrom":[subQ4,makeQuery(id+"F19.opExtrude","CAP_FACE",FACE,{"disambiguationData":[OSD([sQuery(id+"F18.wireOp",EDGE,"E43"),sQuery(id+"F18.wireOp",EDGE,"E45.0"),sQuery(id+"F18.wireOp",EDGE,"E46.0"),subQ5,sQuery(id+"F18.wireOp",EDGE,"E51")])],"isStart":true})]}),makeQuery(id+"F19.boolean.opBoolean","INTERSECT",EDGE,{"derivedFrom":[subQ4,makeQuery(id+"F19.opExtrude","SWEPT_FACE",FACE,{"disambiguationData":[OSD([subQ5])]})]})],"blendedInto":[]});}
            var Q1;
            {var subQ4=sQuery(id+"F18.wireOp",EDGE,"E48");Q1=makeQuery(id+"F21.opFillet","BLEND_EDGE",EDGE,{"blendedFrom":[makeQuery(id+"F19.boolean.opBoolean","INTERSECT",EDGE,{"derivedFrom":[makeQuery(id+"F16.boolean.opBoolean","SPLIT",FACE,{"disambiguationData":[TD([makeQuery(id+"F16.opRevolve","SWEPT_FACE",FACE,{"disambiguationData":[OSD([sQuery(id+"F15.wireOp",EDGE,"E33.0")])]})])],"derivedFrom":makeQuery(id+"F16.opRevolve","SWEPT_FACE",FACE,{"disambiguationData":[OSD([sQuery(id+"F15.wireOp",EDGE,"E36")])]})}),makeQuery(id+"F19.opExtrude","SWEPT_FACE",FACE,{"disambiguationData":[OSD([subQ4])]})]}),makeQuery(id+"F19.opExtrude","CAP_FACE",FACE,{"disambiguationData":[OSD([sQuery(id+"F18.wireOp",EDGE,"E43"),sQuery(id+"F18.wireOp",EDGE,"E45.0"),sQuery(id+"F18.wireOp",EDGE,"E46.0"),subQ4,sQuery(id+"F18.wireOp",EDGE,"E51")])],"isStart":true})],"blendedInto":[makeQuery(id+"F19.opExtrude","CAP_FACE",FACE,{"disambiguationData":[OSD([sQuery(id+"F18.wireOp",EDGE,"E43"),sQuery(id+"F18.wireOp",EDGE,"E45.0"),sQuery(id+"F18.wireOp",EDGE,"E46.0"),subQ4,sQuery(id+"F18.wireOp",EDGE,"E51")])],"isStart":true})]});}
            var Q2;
            Q2=makeQuery(id+"F19.opExtrude","CAP_EDGE",EDGE,{"disambiguationData":[OSD([sQuery(id+"F18.wireOp",EDGE,"E48")])],"isStart":true});
            var Q3;
            Q3=makeQuery(id+"F19.opExtrude","CAP_EDGE",EDGE,{"disambiguationData":[OSD([sQuery(id+"F18.wireOp",EDGE,"E46.0")])],"isStart":true});
            var Q4;
            Q4=makeQuery(id+"F19.opExtrude","CAP_EDGE",EDGE,{"disambiguationData":[OSD([sQuery(id+"F18.wireOp",EDGE,"E51")])],"isStart":true});
            var Q5;
            {var subQ4=sQuery(id+"F18.wireOp",EDGE,"E51");Q5=makeQuery(id+"F21.opFillet","BLEND_EDGE",EDGE,{"blendedFrom":[makeQuery(id+"F19.boolean.opBoolean","INTERSECT",EDGE,{"derivedFrom":[makeQuery(id+"F16.boolean.opBoolean","SPLIT",FACE,{"disambiguationData":[TD([makeQuery(id+"F16.opRevolve","SWEPT_FACE",FACE,{"disambiguationData":[OSD([sQuery(id+"F15.wireOp",EDGE,"E33.0")])]})])],"derivedFrom":makeQuery(id+"F16.opRevolve","SWEPT_FACE",FACE,{"disambiguationData":[OSD([sQuery(id+"F15.wireOp",EDGE,"E36")])]})}),makeQuery(id+"F19.opExtrude","SWEPT_FACE",FACE,{"disambiguationData":[OSD([subQ4])]})]}),makeQuery(id+"F19.opExtrude","CAP_FACE",FACE,{"disambiguationData":[OSD([sQuery(id+"F18.wireOp",EDGE,"E43"),sQuery(id+"F18.wireOp",EDGE,"E45.0"),sQuery(id+"F18.wireOp",EDGE,"E46.0"),sQuery(id+"F18.wireOp",EDGE,"E48"),subQ4])],"isStart":true})],"blendedInto":[makeQuery(id+"F19.opExtrude","CAP_FACE",FACE,{"disambiguationData":[OSD([sQuery(id+"F18.wireOp",EDGE,"E43"),sQuery(id+"F18.wireOp",EDGE,"E45.0"),sQuery(id+"F18.wireOp",EDGE,"E46.0"),sQuery(id+"F18.wireOp",EDGE,"E48"),subQ4])],"isStart":true})]});}
            var Q6;
            {var subQ4=makeQuery(id+"F16.boolean.opBoolean","SPLIT",FACE,{"disambiguationData":[TD([makeQuery(id+"F16.opRevolve","SWEPT_FACE",FACE,{"disambiguationData":[OSD([sQuery(id+"F15.wireOp",EDGE,"E33.0")])]})])],"derivedFrom":makeQuery(id+"F16.opRevolve","SWEPT_FACE",FACE,{"disambiguationData":[OSD([sQuery(id+"F15.wireOp",EDGE,"E36")])]})});var subQ5=sQuery(id+"F18.wireOp",EDGE,"E51");Q6=makeQuery(id+"F21.opFillet","BLEND_EDGE",EDGE,{"blendedFrom":[makeQuery(id+"F19.boolean.opBoolean","INTERSECT",EDGE,{"derivedFrom":[subQ4,makeQuery(id+"F19.opExtrude","CAP_FACE",FACE,{"disambiguationData":[OSD([sQuery(id+"F18.wireOp",EDGE,"E43"),sQuery(id+"F18.wireOp",EDGE,"E45.0"),sQuery(id+"F18.wireOp",EDGE,"E46.0"),sQuery(id+"F18.wireOp",EDGE,"E48"),subQ5])],"isStart":true})]}),makeQuery(id+"F19.boolean.opBoolean","INTERSECT",EDGE,{"derivedFrom":[subQ4,makeQuery(id+"F19.opExtrude","SWEPT_FACE",FACE,{"disambiguationData":[OSD([subQ5])]})]})],"blendedInto":[]});}
            var Q7;
            {var subQ4=makeQuery(id+"F16.boolean.opBoolean","SPLIT",FACE,{"disambiguationData":[TD([makeQuery(id+"F16.opRevolve","SWEPT_FACE",FACE,{"disambiguationData":[OSD([sQuery(id+"F15.wireOp",EDGE,"E33.0")])]})])],"derivedFrom":makeQuery(id+"F16.opRevolve","SWEPT_FACE",FACE,{"disambiguationData":[OSD([sQuery(id+"F15.wireOp",EDGE,"E36")])]})});var subQ5=sQuery(id+"F18.wireOp",EDGE,"E49");Q7=makeQuery(id+"F20.opFillet","BLEND_EDGE",EDGE,{"blendedFrom":[makeQuery(id+"F19.boolean.opBoolean","INTERSECT",EDGE,{"derivedFrom":[subQ4,makeQuery(id+"F19.opExtrude","CAP_FACE",FACE,{"disambiguationData":[OSD([sQuery(id+"F18.wireOp",EDGE,"E45.0"),sQuery(id+"F18.wireOp",EDGE,"E47.2.MirrorC"),sQuery(id+"F18.wireOp",EDGE,"E47.4.MirrorC"),subQ5,sQuery(id+"F18.wireOp",EDGE,"E50")])],"isStart":true})]}),makeQuery(id+"F19.boolean.opBoolean","INTERSECT",EDGE,{"derivedFrom":[subQ4,makeQuery(id+"F19.opExtrude","SWEPT_FACE",FACE,{"disambiguationData":[OSD([subQ5])]})]})],"blendedInto":[]});}
            var Q8;
            {var subQ4=sQuery(id+"F18.wireOp",EDGE,"E49");Q8=makeQuery(id+"F20.opFillet","BLEND_EDGE",EDGE,{"blendedFrom":[makeQuery(id+"F19.boolean.opBoolean","INTERSECT",EDGE,{"derivedFrom":[makeQuery(id+"F16.boolean.opBoolean","SPLIT",FACE,{"disambiguationData":[TD([makeQuery(id+"F16.opRevolve","SWEPT_FACE",FACE,{"disambiguationData":[OSD([sQuery(id+"F15.wireOp",EDGE,"E33.0")])]})])],"derivedFrom":makeQuery(id+"F16.opRevolve","SWEPT_FACE",FACE,{"disambiguationData":[OSD([sQuery(id+"F15.wireOp",EDGE,"E36")])]})}),makeQuery(id+"F19.opExtrude","SWEPT_FACE",FACE,{"disambiguationData":[OSD([subQ4])]})]}),makeQuery(id+"F19.opExtrude","CAP_FACE",FACE,{"disambiguationData":[OSD([sQuery(id+"F18.wireOp",EDGE,"E45.0"),sQuery(id+"F18.wireOp",EDGE,"E47.2.MirrorC"),sQuery(id+"F18.wireOp",EDGE,"E47.4.MirrorC"),subQ4,sQuery(id+"F18.wireOp",EDGE,"E50")])],"isStart":true})],"blendedInto":[makeQuery(id+"F19.opExtrude","CAP_FACE",FACE,{"disambiguationData":[OSD([sQuery(id+"F18.wireOp",EDGE,"E45.0"),sQuery(id+"F18.wireOp",EDGE,"E47.2.MirrorC"),sQuery(id+"F18.wireOp",EDGE,"E47.4.MirrorC"),subQ4,sQuery(id+"F18.wireOp",EDGE,"E50")])],"isStart":true})]});}
            var Q9;
            Q9=makeQuery(id+"F19.opExtrude","CAP_EDGE",EDGE,{"disambiguationData":[OSD([sQuery(id+"F18.wireOp",EDGE,"E49")])],"isStart":true});
            var Q10;
            Q10=makeQuery(id+"F19.opExtrude","CAP_EDGE",EDGE,{"disambiguationData":[OSD([sQuery(id+"F18.wireOp",EDGE,"E47.4.MirrorC")])],"isStart":true});
            var Q11;
            Q11=makeQuery(id+"F19.opExtrude","CAP_EDGE",EDGE,{"disambiguationData":[OSD([sQuery(id+"F18.wireOp",EDGE,"E50")])],"isStart":true});
            var Q12;
            {var subQ4=sQuery(id+"F18.wireOp",EDGE,"E50");Q12=makeQuery(id+"F20.opFillet","BLEND_EDGE",EDGE,{"blendedFrom":[makeQuery(id+"F19.boolean.opBoolean","INTERSECT",EDGE,{"derivedFrom":[makeQuery(id+"F16.boolean.opBoolean","SPLIT",FACE,{"disambiguationData":[TD([makeQuery(id+"F16.opRevolve","SWEPT_FACE",FACE,{"disambiguationData":[OSD([sQuery(id+"F15.wireOp",EDGE,"E33.0")])]})])],"derivedFrom":makeQuery(id+"F16.opRevolve","SWEPT_FACE",FACE,{"disambiguationData":[OSD([sQuery(id+"F15.wireOp",EDGE,"E36")])]})}),makeQuery(id+"F19.opExtrude","SWEPT_FACE",FACE,{"disambiguationData":[OSD([subQ4])]})]}),makeQuery(id+"F19.opExtrude","CAP_FACE",FACE,{"disambiguationData":[OSD([sQuery(id+"F18.wireOp",EDGE,"E45.0"),sQuery(id+"F18.wireOp",EDGE,"E47.2.MirrorC"),sQuery(id+"F18.wireOp",EDGE,"E47.4.MirrorC"),sQuery(id+"F18.wireOp",EDGE,"E49"),subQ4])],"isStart":true})],"blendedInto":[makeQuery(id+"F19.opExtrude","CAP_FACE",FACE,{"disambiguationData":[OSD([sQuery(id+"F18.wireOp",EDGE,"E45.0"),sQuery(id+"F18.wireOp",EDGE,"E47.2.MirrorC"),sQuery(id+"F18.wireOp",EDGE,"E47.4.MirrorC"),sQuery(id+"F18.wireOp",EDGE,"E49"),subQ4])],"isStart":true})]});}
            var Q13;
            {var subQ4=makeQuery(id+"F16.boolean.opBoolean","SPLIT",FACE,{"disambiguationData":[TD([makeQuery(id+"F16.opRevolve","SWEPT_FACE",FACE,{"disambiguationData":[OSD([sQuery(id+"F15.wireOp",EDGE,"E33.0")])]})])],"derivedFrom":makeQuery(id+"F16.opRevolve","SWEPT_FACE",FACE,{"disambiguationData":[OSD([sQuery(id+"F15.wireOp",EDGE,"E36")])]})});var subQ5=sQuery(id+"F18.wireOp",EDGE,"E50");Q13=makeQuery(id+"F20.opFillet","BLEND_EDGE",EDGE,{"blendedFrom":[makeQuery(id+"F19.boolean.opBoolean","INTERSECT",EDGE,{"derivedFrom":[subQ4,makeQuery(id+"F19.opExtrude","CAP_FACE",FACE,{"disambiguationData":[OSD([sQuery(id+"F18.wireOp",EDGE,"E45.0"),sQuery(id+"F18.wireOp",EDGE,"E47.2.MirrorC"),sQuery(id+"F18.wireOp",EDGE,"E47.4.MirrorC"),sQuery(id+"F18.wireOp",EDGE,"E49"),subQ5])],"isStart":true})]}),makeQuery(id+"F19.boolean.opBoolean","INTERSECT",EDGE,{"derivedFrom":[subQ4,makeQuery(id+"F19.opExtrude","SWEPT_FACE",FACE,{"disambiguationData":[OSD([subQ5])]})]})],"blendedInto":[]});}
            fillet(context, id + "F26", {"entities" : qUnion([Q0, Q1, Q2, Q3, Q4, Q5, Q6, Q7, Q8, Q9, Q10, Q11, Q12, Q13]), "radius" : 1 * mm, "tangentPropagation" : true, "allowEdgeOverflow" : false});
        }
        {
            var Q0;
            Q0=makeQuery(id+"F16.opRevolve","SWEPT_EDGE",EDGE,{"disambiguationData":[OSD([sQuery(id+"F15.wireOp",EDGE,"E33.0"),sQuery(id+"F15.wireOp",EDGE,"E36")])]});
            chamfer(context, id + "F27", {"entities" : qUnion([Q0]), "width" : .5 * mm, "tangentPropagation" : true});
        }
        {
            var Q0;
            Q0=makeQuery(id+"F16.opRevolve","SWEPT_EDGE",EDGE,{"disambiguationData":[OSD([sQuery(id+"F15.wireOp",EDGE,"E34.0"),sQuery(id+"F15.wireOp",EDGE,"E36")])]});
            chamfer(context, id + "F28", {"entities" : qUnion([Q0]), "width" : .5 * mm, "tangentPropagation" : true});
        }
        {
            var Q0;
            Q0=qCreatedBy(id+"F17.planeOp",FACE);
            cPlane(context, id + "F29", {"entities" : qUnion([Q0]), "cplaneType" : CPlaneType.OFFSET, "offset" : 90 * mm, "width" : 150 * mm, "height" : 150 * mm});
        }
        {
            var Q0;
            Q0=qCreatedBy(id+"F29.planeOp",FACE);
            var sketch = newSketch(context, id + "F30", { "sketchPlane" : qUnion([Q0])});
            skCircle(sketch, "E52", {"center": v(0, -43.56) * mm, "radius": 3.05 * mm});
            skCircle(sketch, "E53", {"center": v(0, -43.56) * mm, "radius": 5.05 * mm});
            skCircle(sketch, "E54.0", {"center": v(0, -43.56) * mm, "radius": 6.05 * mm});
            skPoint(sketch, "E55.orphan", {"position": v(0, -35.3) * mm});
            skLineSegment(sketch, "E56", {"start": v(0, -43.56) * mm, "end": v(-6.05, -43.56) * mm});
            skLineSegment(sketch, "E57", {"start": v(-6.05, -43.56) * mm, "end": v(0, -43.56) * mm});
            skLineSegment(sketch, "E58", {"start": v(0, -43.56) * mm, "end": v(6.05, -43.56) * mm});
            skLineSegment(sketch, "E59", {"start": v(-6.05, -43.56) * mm, "end": v(-6.05, -35.8) * mm});
            skLineSegment(sketch, "E60", {"start": v(6.05, -43.56) * mm, "end": v(6.05, -35.8) * mm});
            skLineSegment(sketch, "E61.0", {"start": v(6.05, -35.8) * mm, "end": v(-6.05, -35.8) * mm});
            skSolve(sketch);
        }
        {
            var Q0;
            Q0 = qSketchRegion(id + "F30", true);
            var Q1;
            {var subQ0=sQuery(id+"F30.wireOp",EDGE,"E57");var subQ3=sQuery(id+"F30.wireOp",EDGE,"E52");var subQ4=makeQuery(id+"F30.imprint","INTERSECT",VERTEX,{"derivedFrom":[subQ3,subQ0]});Q1=makeQuery(id+"F30.imprint","IMPRINT",FACE,{"disambiguationData":[TD([[makeQuery(id+"F30.imprint","IMPRINT",EDGE,{"disambiguationData":[TD([[subQ4,1.0]])],"derivedFrom":subQ3}),-1.0]])]});}
            var Q2;
            {var subQ3=sQuery(id+"F30.wireOp",EDGE,"E52");var subQ5=sQuery(id+"F30.wireOp",EDGE,"E57");var subQ7=makeQuery(id+"F30.imprint","INTERSECT",VERTEX,{"derivedFrom":[subQ3,subQ5]});Q2=makeQuery(id+"F30.imprint","IMPRINT",FACE,{"disambiguationData":[TD([[makeQuery(id+"F30.imprint","IMPRINT",EDGE,{"disambiguationData":[TD([[subQ7,-1.0]])],"derivedFrom":subQ3}),-1.0]])]});}
            extrude(context, id + "F31", {"entities" : qUnion([Q0, Q1, Q2]), "operationType" : NewBodyOperationType.ADD, "endBound" : BoundingType.SYMMETRIC, "depth" : 15 * mm});
        }
        {
            var Q0;
            {var subQ0=makeQuery(id+"F7.opRevolve","SWEPT_FACE",FACE,{"disambiguationData":[OSD([sQuery(id+"F6.wireOp",EDGE,"E20")])]});var subQ1=sQuery(id+"F30.wireOp",EDGE,"E60");Q0=makeQuery(id+"FCKgpOk4ZCDKGAJ_1.opFillet","BLEND_EDGE",EDGE,{"blendedFrom":[makeQuery(id+"F31.boolean.opBoolean","INTERSECT",EDGE,{"derivedFrom":[subQ0,makeQuery(id+"F31.opExtrude","CAP_FACE",FACE,{"disambiguationData":[OSD([sQuery(id+"F30.wireOp",EDGE,"E52"),sQuery(id+"F30.wireOp",EDGE,"E54.0"),sQuery(id+"F30.wireOp",EDGE,"E59"),subQ1,sQuery(id+"F30.wireOp",EDGE,"E61.0")])],"isStart":false})]}),makeQuery(id+"F31.boolean.opBoolean","INTERSECT",EDGE,{"derivedFrom":[subQ0,makeQuery(id+"F31.opExtrude","SWEPT_FACE",FACE,{"disambiguationData":[OSD([subQ1])]})]})],"blendedInto":[]});}
            var Q1;
            {var subQ0=sQuery(id+"F30.wireOp",EDGE,"E60");Q1=makeQuery(id+"FCKgpOk4ZCDKGAJ_1.opFillet","BLEND_EDGE",EDGE,{"blendedFrom":[makeQuery(id+"F31.boolean.opBoolean","INTERSECT",EDGE,{"derivedFrom":[makeQuery(id+"F7.opRevolve","SWEPT_FACE",FACE,{"disambiguationData":[OSD([sQuery(id+"F6.wireOp",EDGE,"E20")])]}),makeQuery(id+"F31.opExtrude","SWEPT_FACE",FACE,{"disambiguationData":[OSD([subQ0])]})]}),makeQuery(id+"F31.opExtrude","CAP_FACE",FACE,{"disambiguationData":[OSD([sQuery(id+"F30.wireOp",EDGE,"E52"),sQuery(id+"F30.wireOp",EDGE,"E54.0"),sQuery(id+"F30.wireOp",EDGE,"E59"),subQ0,sQuery(id+"F30.wireOp",EDGE,"E61.0")])],"isStart":false})],"blendedInto":[makeQuery(id+"F31.opExtrude","CAP_FACE",FACE,{"disambiguationData":[OSD([sQuery(id+"F30.wireOp",EDGE,"E52"),sQuery(id+"F30.wireOp",EDGE,"E54.0"),sQuery(id+"F30.wireOp",EDGE,"E59"),subQ0,sQuery(id+"F30.wireOp",EDGE,"E61.0")])],"isStart":false})]});}
            var Q2;
            Q2=makeQuery(id+"F31.opExtrude","CAP_EDGE",EDGE,{"disambiguationData":[OSD([sQuery(id+"F30.wireOp",EDGE,"E60")])],"isStart":false});
            var Q3;
            Q3=makeQuery(id+"F31.opExtrude","CAP_EDGE",EDGE,{"disambiguationData":[OSD([sQuery(id+"F30.wireOp",EDGE,"E54.0")])],"isStart":false});
            var Q4;
            Q4=makeQuery(id+"F31.opExtrude","CAP_EDGE",EDGE,{"disambiguationData":[OSD([sQuery(id+"F30.wireOp",EDGE,"E59")])],"isStart":false});
            var Q5;
            {var subQ0=sQuery(id+"F30.wireOp",EDGE,"E59");Q5=makeQuery(id+"FCKgpOk4ZCDKGAJ_1.opFillet","BLEND_EDGE",EDGE,{"blendedFrom":[makeQuery(id+"F31.boolean.opBoolean","INTERSECT",EDGE,{"derivedFrom":[makeQuery(id+"F7.opRevolve","SWEPT_FACE",FACE,{"disambiguationData":[OSD([sQuery(id+"F6.wireOp",EDGE,"E22.0.MirrorCS")])]}),makeQuery(id+"F31.opExtrude","SWEPT_FACE",FACE,{"disambiguationData":[OSD([subQ0])]})]}),makeQuery(id+"F31.opExtrude","CAP_FACE",FACE,{"disambiguationData":[OSD([sQuery(id+"F30.wireOp",EDGE,"E52"),sQuery(id+"F30.wireOp",EDGE,"E54.0"),subQ0,sQuery(id+"F30.wireOp",EDGE,"E60"),sQuery(id+"F30.wireOp",EDGE,"E61.0")])],"isStart":false})],"blendedInto":[makeQuery(id+"F31.opExtrude","CAP_FACE",FACE,{"disambiguationData":[OSD([sQuery(id+"F30.wireOp",EDGE,"E52"),sQuery(id+"F30.wireOp",EDGE,"E54.0"),subQ0,sQuery(id+"F30.wireOp",EDGE,"E60"),sQuery(id+"F30.wireOp",EDGE,"E61.0")])],"isStart":false})]});}
            var Q6;
            {var subQ0=makeQuery(id+"F7.opRevolve","SWEPT_FACE",FACE,{"disambiguationData":[OSD([sQuery(id+"F6.wireOp",EDGE,"E22.0.MirrorCS")])]});var subQ1=sQuery(id+"F30.wireOp",EDGE,"E59");Q6=makeQuery(id+"FCKgpOk4ZCDKGAJ_1.opFillet","BLEND_EDGE",EDGE,{"blendedFrom":[makeQuery(id+"F31.boolean.opBoolean","INTERSECT",EDGE,{"derivedFrom":[subQ0,makeQuery(id+"F31.opExtrude","CAP_FACE",FACE,{"disambiguationData":[OSD([sQuery(id+"F30.wireOp",EDGE,"E52"),sQuery(id+"F30.wireOp",EDGE,"E54.0"),subQ1,sQuery(id+"F30.wireOp",EDGE,"E60"),sQuery(id+"F30.wireOp",EDGE,"E61.0")])],"isStart":false})]}),makeQuery(id+"F31.boolean.opBoolean","INTERSECT",EDGE,{"derivedFrom":[subQ0,makeQuery(id+"F31.opExtrude","SWEPT_FACE",FACE,{"disambiguationData":[OSD([subQ1])]})]})],"blendedInto":[]});}
            var Q7;
            {var subQ0=makeQuery(id+"F7.opRevolve","SWEPT_FACE",FACE,{"disambiguationData":[OSD([sQuery(id+"F6.wireOp",EDGE,"E20")])]});var subQ1=sQuery(id+"F30.wireOp",EDGE,"E60");Q7=makeQuery(id+"FCKgpOk4ZCDKGAJ_1.opFillet","BLEND_EDGE",EDGE,{"blendedFrom":[makeQuery(id+"F31.boolean.opBoolean","INTERSECT",EDGE,{"derivedFrom":[subQ0,makeQuery(id+"F31.opExtrude","CAP_FACE",FACE,{"disambiguationData":[OSD([sQuery(id+"F30.wireOp",EDGE,"E52"),sQuery(id+"F30.wireOp",EDGE,"E54.0"),sQuery(id+"F30.wireOp",EDGE,"E59"),subQ1,sQuery(id+"F30.wireOp",EDGE,"E61.0")])],"isStart":true})]}),makeQuery(id+"F31.boolean.opBoolean","INTERSECT",EDGE,{"derivedFrom":[subQ0,makeQuery(id+"F31.opExtrude","SWEPT_FACE",FACE,{"disambiguationData":[OSD([subQ1])]})]})],"blendedInto":[]});}
            var Q8;
            {var subQ0=sQuery(id+"F30.wireOp",EDGE,"E60");Q8=makeQuery(id+"FCKgpOk4ZCDKGAJ_1.opFillet","BLEND_EDGE",EDGE,{"blendedFrom":[makeQuery(id+"F31.boolean.opBoolean","INTERSECT",EDGE,{"derivedFrom":[makeQuery(id+"F7.opRevolve","SWEPT_FACE",FACE,{"disambiguationData":[OSD([sQuery(id+"F6.wireOp",EDGE,"E20")])]}),makeQuery(id+"F31.opExtrude","SWEPT_FACE",FACE,{"disambiguationData":[OSD([subQ0])]})]}),makeQuery(id+"F31.opExtrude","CAP_FACE",FACE,{"disambiguationData":[OSD([sQuery(id+"F30.wireOp",EDGE,"E52"),sQuery(id+"F30.wireOp",EDGE,"E54.0"),sQuery(id+"F30.wireOp",EDGE,"E59"),subQ0,sQuery(id+"F30.wireOp",EDGE,"E61.0")])],"isStart":true})],"blendedInto":[makeQuery(id+"F31.opExtrude","CAP_FACE",FACE,{"disambiguationData":[OSD([sQuery(id+"F30.wireOp",EDGE,"E52"),sQuery(id+"F30.wireOp",EDGE,"E54.0"),sQuery(id+"F30.wireOp",EDGE,"E59"),subQ0,sQuery(id+"F30.wireOp",EDGE,"E61.0")])],"isStart":true})]});}
            var Q9;
            Q9=makeQuery(id+"F31.opExtrude","CAP_EDGE",EDGE,{"disambiguationData":[OSD([sQuery(id+"F30.wireOp",EDGE,"E60")])],"isStart":true});
            var Q10;
            Q10=makeQuery(id+"F31.opExtrude","CAP_EDGE",EDGE,{"disambiguationData":[OSD([sQuery(id+"F30.wireOp",EDGE,"E54.0")])],"isStart":true});
            var Q11;
            Q11=makeQuery(id+"F31.opExtrude","CAP_EDGE",EDGE,{"disambiguationData":[OSD([sQuery(id+"F30.wireOp",EDGE,"E59")])],"isStart":true});
            var Q12;
            {var subQ0=sQuery(id+"F30.wireOp",EDGE,"E59");Q12=makeQuery(id+"FCKgpOk4ZCDKGAJ_1.opFillet","BLEND_EDGE",EDGE,{"blendedFrom":[makeQuery(id+"F31.boolean.opBoolean","INTERSECT",EDGE,{"derivedFrom":[makeQuery(id+"F7.opRevolve","SWEPT_FACE",FACE,{"disambiguationData":[OSD([sQuery(id+"F6.wireOp",EDGE,"E22.0.MirrorCS")])]}),makeQuery(id+"F31.opExtrude","SWEPT_FACE",FACE,{"disambiguationData":[OSD([subQ0])]})]}),makeQuery(id+"F31.opExtrude","CAP_FACE",FACE,{"disambiguationData":[OSD([sQuery(id+"F30.wireOp",EDGE,"E52"),sQuery(id+"F30.wireOp",EDGE,"E54.0"),subQ0,sQuery(id+"F30.wireOp",EDGE,"E60"),sQuery(id+"F30.wireOp",EDGE,"E61.0")])],"isStart":true})],"blendedInto":[makeQuery(id+"F31.opExtrude","CAP_FACE",FACE,{"disambiguationData":[OSD([sQuery(id+"F30.wireOp",EDGE,"E52"),sQuery(id+"F30.wireOp",EDGE,"E54.0"),subQ0,sQuery(id+"F30.wireOp",EDGE,"E60"),sQuery(id+"F30.wireOp",EDGE,"E61.0")])],"isStart":true})]});}
            var Q13;
            {var subQ0=makeQuery(id+"F7.opRevolve","SWEPT_FACE",FACE,{"disambiguationData":[OSD([sQuery(id+"F6.wireOp",EDGE,"E22.0.MirrorCS")])]});var subQ1=sQuery(id+"F30.wireOp",EDGE,"E59");Q13=makeQuery(id+"FCKgpOk4ZCDKGAJ_1.opFillet","BLEND_EDGE",EDGE,{"blendedFrom":[makeQuery(id+"F31.boolean.opBoolean","INTERSECT",EDGE,{"derivedFrom":[subQ0,makeQuery(id+"F31.opExtrude","CAP_FACE",FACE,{"disambiguationData":[OSD([sQuery(id+"F30.wireOp",EDGE,"E52"),sQuery(id+"F30.wireOp",EDGE,"E54.0"),subQ1,sQuery(id+"F30.wireOp",EDGE,"E60"),sQuery(id+"F30.wireOp",EDGE,"E61.0")])],"isStart":true})]}),makeQuery(id+"F31.boolean.opBoolean","INTERSECT",EDGE,{"derivedFrom":[subQ0,makeQuery(id+"F31.opExtrude","SWEPT_FACE",FACE,{"disambiguationData":[OSD([subQ1])]})]})],"blendedInto":[]});}
            fillet(context, id + "F32", {"entities" : qUnion([Q0, Q1, Q2, Q3, Q4, Q5, Q6, Q7, Q8, Q9, Q10, Q11, Q12, Q13]), "radius" : 1 * mm, "tangentPropagation" : true, "allowEdgeOverflow" : false});
        }
        {
            var Q0;
            Q0=makeQuery(id+"F19.opExtrude","CAP_FACE",FACE,{"disambiguationData":[OSD([sQuery(id+"F18.wireOp",EDGE,"E45.0"),sQuery(id+"F18.wireOp",EDGE,"E47.2.MirrorC"),sQuery(id+"F18.wireOp",EDGE,"E47.4.MirrorC"),sQuery(id+"F18.wireOp",EDGE,"E49"),sQuery(id+"F18.wireOp",EDGE,"E50")])],"isStart":true});
            var sketch = newSketch(context, id + "F33", { "sketchPlane" : qUnion([Q0])});
            skCircle(sketch, "E62.0", {"center": v(62.69, -25.94) * mm, "radius": 5.1 * mm});
            skCircle(sketch, "E63.0", {"center": v(70.57, -7.56) * mm, "radius": 5.1 * mm});
            skSolve(sketch);
        }
        {
            var Q0;
            Q0=makeQuery(id+"F33.imprint","IMPRINT",FACE,{"disambiguationData":[TD([[makeQuery(id+"F33.imprint","IMPRINT",EDGE,{"derivedFrom":sQuery(id+"F33.wireOp",EDGE,"E62.0")}),1.0]])]});
            var Q1;
            Q1=makeQuery(id+"F33.imprint","IMPRINT",FACE,{"disambiguationData":[TD([[makeQuery(id+"F33.imprint","IMPRINT",EDGE,{"derivedFrom":sQuery(id+"F33.wireOp",EDGE,"E63.0")}),1.0]])]});
            extrude(context, id + "F34", {"entities" : qUnion([Q0, Q1]), "operationType" : NewBodyOperationType.REMOVE, "oppositeDirection" : true, "depth" : 5 * mm});
        }
        {
            var Q0;
            Q0=makeQuery(id+"F31.opExtrude","CAP_FACE",FACE,{"disambiguationData":[OSD([sQuery(id+"F30.wireOp",EDGE,"E52"),sQuery(id+"F30.wireOp",EDGE,"E54.0"),sQuery(id+"F30.wireOp",EDGE,"E59"),sQuery(id+"F30.wireOp",EDGE,"E60"),sQuery(id+"F30.wireOp",EDGE,"E61.0")])],"isStart":false});
            var sketch = newSketch(context, id + "F35", { "sketchPlane" : qUnion([Q0])});
            skCircle(sketch, "E64.0", {"center": v(0, -43.56) * mm, "radius": 5.05 * mm});
            skSolve(sketch);
        }
        {
            var Q0;
            {var subQ0=sQuery(id+"F30.wireOp",EDGE,"E52");Q0=makeQuery(id+"F35.imprint","IMPRINT",FACE,{"disambiguationData":[TD([[makeQuery(id+"F35.imprint","IMPRINT",EDGE,{"derivedFrom":makeQuery(id+"F31.opExtrude","CAP_EDGE",EDGE,{"disambiguationData":[OSD([subQ0])],"isStart":false})}),-1.0]])]});}
            var Q1;
            Q1=sQuery(id+"F35.wireOp",EDGE,"E64.0");
            extrude(context, id + "F36", {"entities" : qUnion([Q0]), "operationType" : NewBodyOperationType.REMOVE, "surfaceEntities" : qUnion([Q1]), "oppositeDirection" : true, "depth" : 5 * mm});
        }
        {
            var Q0;
            Q0=makeQuery(id+"F31.boolean.opBoolean","INTERSECT",EDGE,{"derivedFrom":[makeQuery(id+"F7.opRevolve","SWEPT_FACE",FACE,{"disambiguationData":[OSD([sQuery(id+"F6.wireOp",EDGE,"E22.0.MirrorCS")])]}),makeQuery(id+"F31.opExtrude","SWEPT_FACE",FACE,{"disambiguationData":[OSD([sQuery(id+"F30.wireOp",EDGE,"E59")])]})]});
            var Q1;
            Q1=makeQuery(id+"F32.opFillet","BLEND_EDGE",EDGE,{"blendedFrom":[makeQuery(id+"F31.opExtrude","CAP_EDGE",EDGE,{"disambiguationData":[OSD([sQuery(id+"F30.wireOp",EDGE,"E59")])],"isStart":false}),makeQuery(id+"F7.opRevolve","SWEPT_FACE",FACE,{"disambiguationData":[OSD([sQuery(id+"F6.wireOp",EDGE,"E22.0.MirrorCS")])]})],"blendedInto":[makeQuery(id+"F7.opRevolve","SWEPT_FACE",FACE,{"disambiguationData":[OSD([sQuery(id+"F6.wireOp",EDGE,"E22.0.MirrorCS")])]})]});
            var Q2;
            Q2=makeQuery(id+"F31.boolean.opBoolean","INTERSECT",EDGE,{"derivedFrom":[makeQuery(id+"F7.opRevolve","SWEPT_FACE",FACE,{"disambiguationData":[OSD([sQuery(id+"F6.wireOp",EDGE,"E22.0.MirrorCS")])]}),makeQuery(id+"F31.opExtrude","CAP_FACE",FACE,{"disambiguationData":[OSD([sQuery(id+"F30.wireOp",EDGE,"E52"),sQuery(id+"F30.wireOp",EDGE,"E54.0"),sQuery(id+"F30.wireOp",EDGE,"E59"),sQuery(id+"F30.wireOp",EDGE,"E60"),sQuery(id+"F30.wireOp",EDGE,"E61.0")])],"isStart":false})]});
            var Q3;
            Q3=makeQuery(id+"F31.boolean.opBoolean","INTERSECT",EDGE,{"derivedFrom":[makeQuery(id+"F7.opRevolve","SWEPT_FACE",FACE,{"disambiguationData":[OSD([sQuery(id+"F6.wireOp",EDGE,"E20")])]}),makeQuery(id+"F31.opExtrude","CAP_FACE",FACE,{"disambiguationData":[OSD([sQuery(id+"F30.wireOp",EDGE,"E52"),sQuery(id+"F30.wireOp",EDGE,"E54.0"),sQuery(id+"F30.wireOp",EDGE,"E59"),sQuery(id+"F30.wireOp",EDGE,"E60"),sQuery(id+"F30.wireOp",EDGE,"E61.0")])],"isStart":false})]});
            var Q4;
            Q4=makeQuery(id+"F32.opFillet","BLEND_EDGE",EDGE,{"blendedFrom":[makeQuery(id+"F31.opExtrude","CAP_EDGE",EDGE,{"disambiguationData":[OSD([sQuery(id+"F30.wireOp",EDGE,"E59")])],"isStart":true}),makeQuery(id+"F7.opRevolve","SWEPT_FACE",FACE,{"disambiguationData":[OSD([sQuery(id+"F6.wireOp",EDGE,"E22.0.MirrorCS")])]})],"blendedInto":[makeQuery(id+"F7.opRevolve","SWEPT_FACE",FACE,{"disambiguationData":[OSD([sQuery(id+"F6.wireOp",EDGE,"E22.0.MirrorCS")])]})]});
            var Q5;
            Q5=makeQuery(id+"F31.boolean.opBoolean","INTERSECT",EDGE,{"derivedFrom":[makeQuery(id+"F7.opRevolve","SWEPT_FACE",FACE,{"disambiguationData":[OSD([sQuery(id+"F6.wireOp",EDGE,"E22.0.MirrorCS")])]}),makeQuery(id+"F31.opExtrude","CAP_FACE",FACE,{"disambiguationData":[OSD([sQuery(id+"F30.wireOp",EDGE,"E52"),sQuery(id+"F30.wireOp",EDGE,"E54.0"),sQuery(id+"F30.wireOp",EDGE,"E59"),sQuery(id+"F30.wireOp",EDGE,"E60"),sQuery(id+"F30.wireOp",EDGE,"E61.0")])],"isStart":true})]});
            var Q6;
            Q6=makeQuery(id+"F31.boolean.opBoolean","INTERSECT",EDGE,{"derivedFrom":[makeQuery(id+"F7.opRevolve","SWEPT_FACE",FACE,{"disambiguationData":[OSD([sQuery(id+"F6.wireOp",EDGE,"E20")])]}),makeQuery(id+"F31.opExtrude","CAP_FACE",FACE,{"disambiguationData":[OSD([sQuery(id+"F30.wireOp",EDGE,"E52"),sQuery(id+"F30.wireOp",EDGE,"E54.0"),sQuery(id+"F30.wireOp",EDGE,"E59"),sQuery(id+"F30.wireOp",EDGE,"E60"),sQuery(id+"F30.wireOp",EDGE,"E61.0")])],"isStart":true})]});
            var Q7;
            Q7=makeQuery(id+"F32.opFillet","BLEND_EDGE",EDGE,{"blendedFrom":[makeQuery(id+"F31.opExtrude","CAP_EDGE",EDGE,{"disambiguationData":[OSD([sQuery(id+"F30.wireOp",EDGE,"E60")])],"isStart":true}),makeQuery(id+"F7.opRevolve","SWEPT_FACE",FACE,{"disambiguationData":[OSD([sQuery(id+"F6.wireOp",EDGE,"E20")])]})],"blendedInto":[makeQuery(id+"F7.opRevolve","SWEPT_FACE",FACE,{"disambiguationData":[OSD([sQuery(id+"F6.wireOp",EDGE,"E20")])]})]});
            var Q8;
            Q8=makeQuery(id+"F31.boolean.opBoolean","INTERSECT",EDGE,{"derivedFrom":[makeQuery(id+"F7.opRevolve","SWEPT_FACE",FACE,{"disambiguationData":[OSD([sQuery(id+"F6.wireOp",EDGE,"E20")])]}),makeQuery(id+"F31.opExtrude","SWEPT_FACE",FACE,{"disambiguationData":[OSD([sQuery(id+"F30.wireOp",EDGE,"E60")])]})]});
            var Q9;
            Q9=makeQuery(id+"F32.opFillet","BLEND_EDGE",EDGE,{"blendedFrom":[makeQuery(id+"F31.opExtrude","CAP_EDGE",EDGE,{"disambiguationData":[OSD([sQuery(id+"F30.wireOp",EDGE,"E60")])],"isStart":false}),makeQuery(id+"F7.opRevolve","SWEPT_FACE",FACE,{"disambiguationData":[OSD([sQuery(id+"F6.wireOp",EDGE,"E20")])]})],"blendedInto":[makeQuery(id+"F7.opRevolve","SWEPT_FACE",FACE,{"disambiguationData":[OSD([sQuery(id+"F6.wireOp",EDGE,"E20")])]})]});
            fillet(context, id + "F37", {"entities" : qUnion([Q0, Q1, Q2, Q3, Q4, Q5, Q6, Q7, Q8, Q9]), "radius" : 5 * mm, "tangentPropagation" : true, "allowEdgeOverflow" : false});
        }
        {
            var Q0;
            Q0=qCreatedBy(id+"F14.planeOp",FACE);
            var sketch = newSketch(context, id + "F38", { "sketchPlane" : qUnion([Q0])});
            skCircle(sketch, "E65", {"center": v(0, 0) * mm, "radius": 6.35 * mm});
            skSolve(sketch);
        }
        {
            var Q0;
            Q0 = qSketchRegion(id + "F38", true);
            extrude(context, id + "F39", {"entities" : qUnion([Q0]), "operationType" : NewBodyOperationType.ADD, "endBound" : BoundingType.SYMMETRIC, "depth" : 24 * mm});
        }
        {
            var Q0;
            {var subQ0=sQuery(id+"F0.wireOp",EDGE,"E1");var subQ1=sQuery(id+"F0.wireOp",EDGE,"E2.0.MirrorCS");var subQ2=sQuery(id+"F0.wireOp",EDGE,"E3");var subQ3=sQuery(id+"F2.wireOp",EDGE,"E8");Q0=makeQuery(id+"F39.boolean.opBoolean","INTERSECT",EDGE,{"disambiguationData":[OD(0.0)],"derivedFrom":[makeQuery(id+"F7.boolean.opBoolean","SPLIT",FACE,{"disambiguationData":[TD([makeQuery(id+"F5.opLoft","SWEPT_FACE",FACE,{"disambiguationData":[OSD([subQ0,subQ1,subQ2,sQuery(id+"F0.wireOp",EDGE,"E5.filletArc"),subQ3])]}),makeQuery(id+"F5.opLoft","CAP_FACE",FACE,{"disambiguationData":[OSD([makeQuery(id+"F4.imprint","IMPRINT",FACE,{"disambiguationData":[TD([[makeQuery(id+"F4.imprint","IMPRINT",EDGE,{"derivedFrom":sQuery(id+"F4.wireOp",EDGE,"E11")}),1.0]])]})])],"isStart":true}),makeQuery(id+"F7.opRevolve","SWEPT_FACE",FACE,{"disambiguationData":[OSD([sQuery(id+"F6.wireOp",EDGE,"E20")])]}),makeQuery(id+"F7.opRevolve","SWEPT_FACE",FACE,{"disambiguationData":[OSD([sQuery(id+"F6.wireOp",EDGE,"E22.0.MirrorCS")])]})])],"derivedFrom":makeQuery(id+"F5.opLoft","SWEPT_FACE",FACE,{"disambiguationData":[OSD([subQ0,subQ1,subQ2,sQuery(id+"F0.wireOp",EDGE,"E4.filletArc"),subQ3])]})}),makeQuery(id+"F39.opExtrude","SWEPT_FACE",FACE,{"disambiguationData":[OSD([sQuery(id+"F38.wireOp",EDGE,"E65")])]})]});}
            fillet(context, id + "F40", {"entities" : qUnion([Q0]), "radius" : 1 * mm, "tangentPropagation" : true, "allowEdgeOverflow" : false});
        }
        {
            var Q0;
            {var subQ0=sQuery(id+"F0.wireOp",EDGE,"E1");var subQ1=sQuery(id+"F0.wireOp",EDGE,"E2.0.MirrorCS");var subQ2=sQuery(id+"F0.wireOp",EDGE,"E3");var subQ3=sQuery(id+"F2.wireOp",EDGE,"E8");Q0=makeQuery(id+"F39.boolean.opBoolean","INTERSECT",EDGE,{"disambiguationData":[OD(1.0)],"derivedFrom":[makeQuery(id+"F7.boolean.opBoolean","SPLIT",FACE,{"disambiguationData":[TD([makeQuery(id+"F5.opLoft","SWEPT_FACE",FACE,{"disambiguationData":[OSD([subQ0,subQ1,subQ2,sQuery(id+"F0.wireOp",EDGE,"E5.filletArc"),subQ3])]}),makeQuery(id+"F5.opLoft","CAP_FACE",FACE,{"disambiguationData":[OSD([makeQuery(id+"F4.imprint","IMPRINT",FACE,{"disambiguationData":[TD([[makeQuery(id+"F4.imprint","IMPRINT",EDGE,{"derivedFrom":sQuery(id+"F4.wireOp",EDGE,"E11")}),1.0]])]})])],"isStart":true}),makeQuery(id+"F7.opRevolve","SWEPT_FACE",FACE,{"disambiguationData":[OSD([sQuery(id+"F6.wireOp",EDGE,"E20")])]}),makeQuery(id+"F7.opRevolve","SWEPT_FACE",FACE,{"disambiguationData":[OSD([sQuery(id+"F6.wireOp",EDGE,"E22.0.MirrorCS")])]})])],"derivedFrom":makeQuery(id+"F5.opLoft","SWEPT_FACE",FACE,{"disambiguationData":[OSD([subQ0,subQ1,subQ2,sQuery(id+"F0.wireOp",EDGE,"E4.filletArc"),subQ3])]})}),makeQuery(id+"F39.opExtrude","SWEPT_FACE",FACE,{"disambiguationData":[OSD([sQuery(id+"F38.wireOp",EDGE,"E65")])]})]});}
            fillet(context, id + "F41", {"entities" : qUnion([Q0]), "radius" : 1 * mm, "tangentPropagation" : true, "allowEdgeOverflow" : false});
        }
    });
